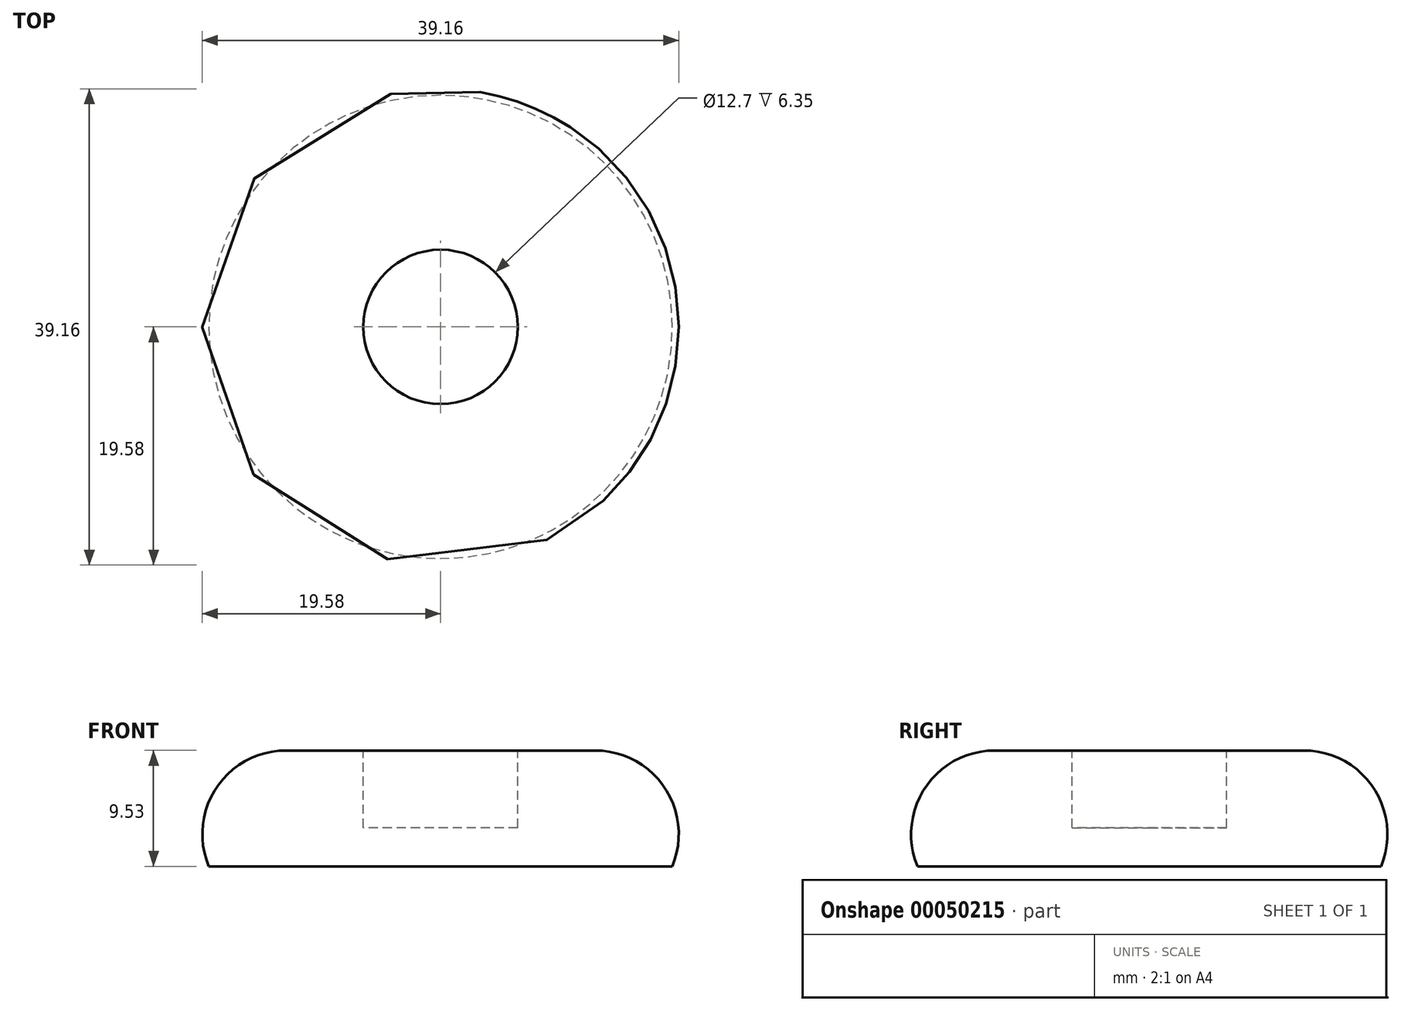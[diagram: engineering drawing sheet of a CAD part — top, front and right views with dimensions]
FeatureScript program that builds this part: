
annotation { "Feature Type Name" : "Feature", "Feature Type Description" : "" }
export const myFeature = defineFeature(function(context is Context, id is Id, definition is map)
    precondition{}
    {
        {
            var Q0;
            Q0=qCreatedBy(makeId("Front.planeOp"),FACE);
            var sketch = newSketch(context, id + "F0", { "sketchPlane" : qUnion([Q0])});
            skLineSegment(sketch, "E0", {"start": v(0, 0) * mm, "end": v(19.05, 0) * mm});
            skLineSegment(sketch, "E1", {"start": v(0, 9.53) * mm, "end": v(12.7, 9.53) * mm});
            skLineSegment(sketch, "E2", {"start": v(0, 0) * mm, "end": v(0, 9.53) * mm});
            skArc(sketch, "E3", {"start": v(12.7, 9.53) * mm, "mid": v(18.42, 6.46) * mm, "end": v(19.05, 0) * mm});
            skLineSegment(sketch, "E4", {"start": v(0, 19.25) * mm, "end": v(0, -14.98) * mm, "construction": true});
            skPoint(sketch, "E4.endSnap0", {"position": v(0, 4.76) * mm});
            skSolve(sketch);
        }
        {
            var Q0;
            Q0=qSketchRegion(id+"F0",true);
            var Q1;
            Q1=sQuery(id+"F0.wireOp",EDGE,"E4");
            revolve(context, id + "F1", {"entities" : qUnion([Q0]), "axis" : qUnion([Q1]), "revolveType" : RevolveType.FULL});
        }
        {
            var Q0;
            Q0=makeQuery(id+"F1.opRevolve","SWEPT_FACE",FACE,{"disambiguationData":[OSD([sQuery(id+"F0.wireOp",EDGE,"E1")])]});
            var sketch = newSketch(context, id + "F2", { "sketchPlane" : qUnion([Q0])});
            skCircle(sketch, "E5", {"center": v(0, 0) * mm, "radius": 6.35 * mm});
            skSolve(sketch);
        }
        {
            var Q0;
            Q0=qSketchRegion(id+"F2",true);
            extrude(context, id + "F3", {"entities" : qUnion([Q0]), "operationType" : NewBodyOperationType.REMOVE, "oppositeDirection" : true, "depth" : 6.35 * mm});
        }
    });
